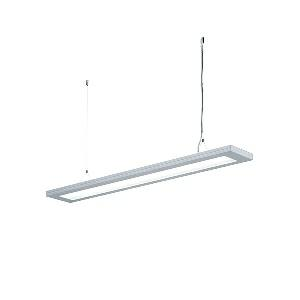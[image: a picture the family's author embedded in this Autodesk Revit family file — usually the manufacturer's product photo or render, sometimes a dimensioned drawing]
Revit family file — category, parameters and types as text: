
# Revit family: lavigo_-_dpp_16000_840_d_g2_00750548_6fff
name_source: partatom
category: Lighting Fixtures
units: mm (PartAtom-declared; Revit-internal decimal feet)

## family parameters
Cut with Voids When Loaded = No
Host = Face
Light Source = No
Part Type = Normal
Room Calculation Point = No
Round Connector Dimension = Use Diameter
Shared = No

## types (1)
- LAVIGO - DPP 16000/840/D/G2 (1 x LED, 16450 lm, 4000K)
    Apparent Load = 112 VA
    Approval mark = CE
    CIE Flux Codes = 60 87 97 11 100
    Color Rendering = 80-89
    Color Temperature = 4000K
    Control Gear = Electronic ballast
    Default Elevation = 1800 mm
    Description = DPP 16000/840/D/G2|Suspended luminaire|light source: LED|connected load: 220-240V, 50/60Hz|Power consumption: approx. 112 W|standby: approx. 0,50|luminous flux: 16450 lm|luminous efficacy: 146 lm/W|light distribution: Direct/indirect|direct ratio: approx. 11 %|colour temperature: Cold white, ca. 4000 K|color rendering index (CRI): >= 80|chromaticity tolerance:  3 SDCM|System of protection: IP 20|technology: Continuously dimmable|luminaire body|material: Steel/plastic|surface: Powder coatet|colour: Silver metallic|lamp cover: Polycarbonate (PC), Clear|mains lead: 1.00 m With free stranded wires|Fastening: Steel cable 0.3 - 0.7 m|decorative contrast side parts: Flint grey|glare control: Prism aperture|luminance(L65): <= 2800 cd/m|unified glare rating(4H 8H): <=  16|special features: Canopy colour (pure white), Cradle to Cradle Certified TM, DALI - dimming via digital rotary dimmer, DALI Load 3x, Direct light component with edge light and light-guide technology for homogenous light exit, Integration into DALI light management systems, Flicker-free, TouchDIM - dimming via standard switch|
    Frequency = 50 Hz
    Height = 36 mm
    Lamp = 1 x LED
    Lamp Light Flux = 16450 lm
    Lamp count = 1
    Length = 1245 mm
    Luminous efficacy = 147 lm/W
    Manufacturer = Waldmann
    ModVariant = No
    Model = 00750548
    Mounting Place = Ceiling
    Mounting Type = Pendant
    Number of Poles = 1
    OnlyDefault = Yes
    Power Factor = 1
    Product Name = LAVIGO - DPP 16000/840/D/G2
    Product group = Suspended luminaire
    ProductGroupID = 9
    Protection Class = Protection class I
    Protection Degree = IP 20
    RLX_Detail_Level = 1
    RLX_Emergency_Light_Flux = 0 lm
    RLX_Emergency_Type = 0
    RLX_Emergency_Type_DB = No
    RlxData = <blob elided: 25129 chars, md5=73f9f0f8>
    Socket = socket
    Standby Power = 0 W
    System Light Flux = 16451 lm
    System Power = 112 W
    Type Comments = Product without accessories
    Type Image = 121740000-00678747.jpg
    URL = http://relux.com
    VarID = ---
    Voltage = 230 V
    Voltage Range = 220-240 V
    Weight = 0.00 kg
    Width = 200 mm  [stored 0.656168 ft]

note: [stored X ft] marks values corroborated as IEEE doubles in the binary element streams (Revit-internal decimal feet)

## geometry (parser evidence)
native form markers: Blend x4, Sweep x15
no freeform markers — native parametric forms only
